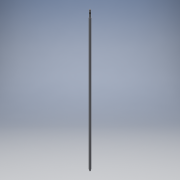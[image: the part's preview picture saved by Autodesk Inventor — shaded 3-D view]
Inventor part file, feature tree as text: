
AUTODESK INVENTOR PART (.ipt)
format: ipt  version: 2018 (Build 220112000, 112)  size: 121,856 bytes
history: native  units: mm
features: extrude x6, sketch x6, other x1, thread x1, chamfer x1
ambient origin geometry x8: Origin, YZ Plane, XZ Plane, XY Plane, X Axis, Y Axis, Z Axis, Center Point
bodies: Body1 (feature_tree)
feature tree (15):
  other  "Sólido1"
  extrude  "Extrusão1"  Depth=1015.0mm TaperAngle=0.0deg
  extrude  "Extrusão2"  Depth=39.0mm TaperAngle=0.0deg
  extrude  "Extrusão3"  Depth=15.0mm TaperAngle=0.0deg
  extrude  "Extrusão4"  Depth=9.15mm TaperAngle=0.0deg
  extrude  "Extrusão5"  Depth=1.15mm TaperAngle=0.0deg
  extrude  "Extrusão6"  Depth=1.85mm TaperAngle=0.0deg
  thread  "Rosca1"  [1 undecoded]
  chamfer  "Chanfro1"  Distance=0.5mm Angle=45.0deg
  sketch  "Esboço1"  dims[d0=16.0mm d1=1015.0mm d2=0.0mm]
  sketch  "Esboço2"  dims[d3=12.0mm d4=39.0mm d5=0.0mm]
  sketch  "Esboço3"  dims[d6=10.0mm d7=15.0mm d8=0.0mm]
  sketch  "Esboço4"  dims[d9=10.0mm d10=9.15mm d11=0.0mm]
  sketch  "Esboço5"  dims[d12=9.0mm d13=1.15mm d14=0.0mm]
  sketch  "Esboço6"  dims[d15=10.0mm d16=1.85mm d17=0.0mm d18=14.0mm d19=0.0mm d20=0.5mm d21=2.0mm d22=45.0deg]
note: 1 required parameter value undecoded (feature->parameter linkage not recoverable at this tier; creation-order binding heuristic only, values carry confidence <= 0.55)
